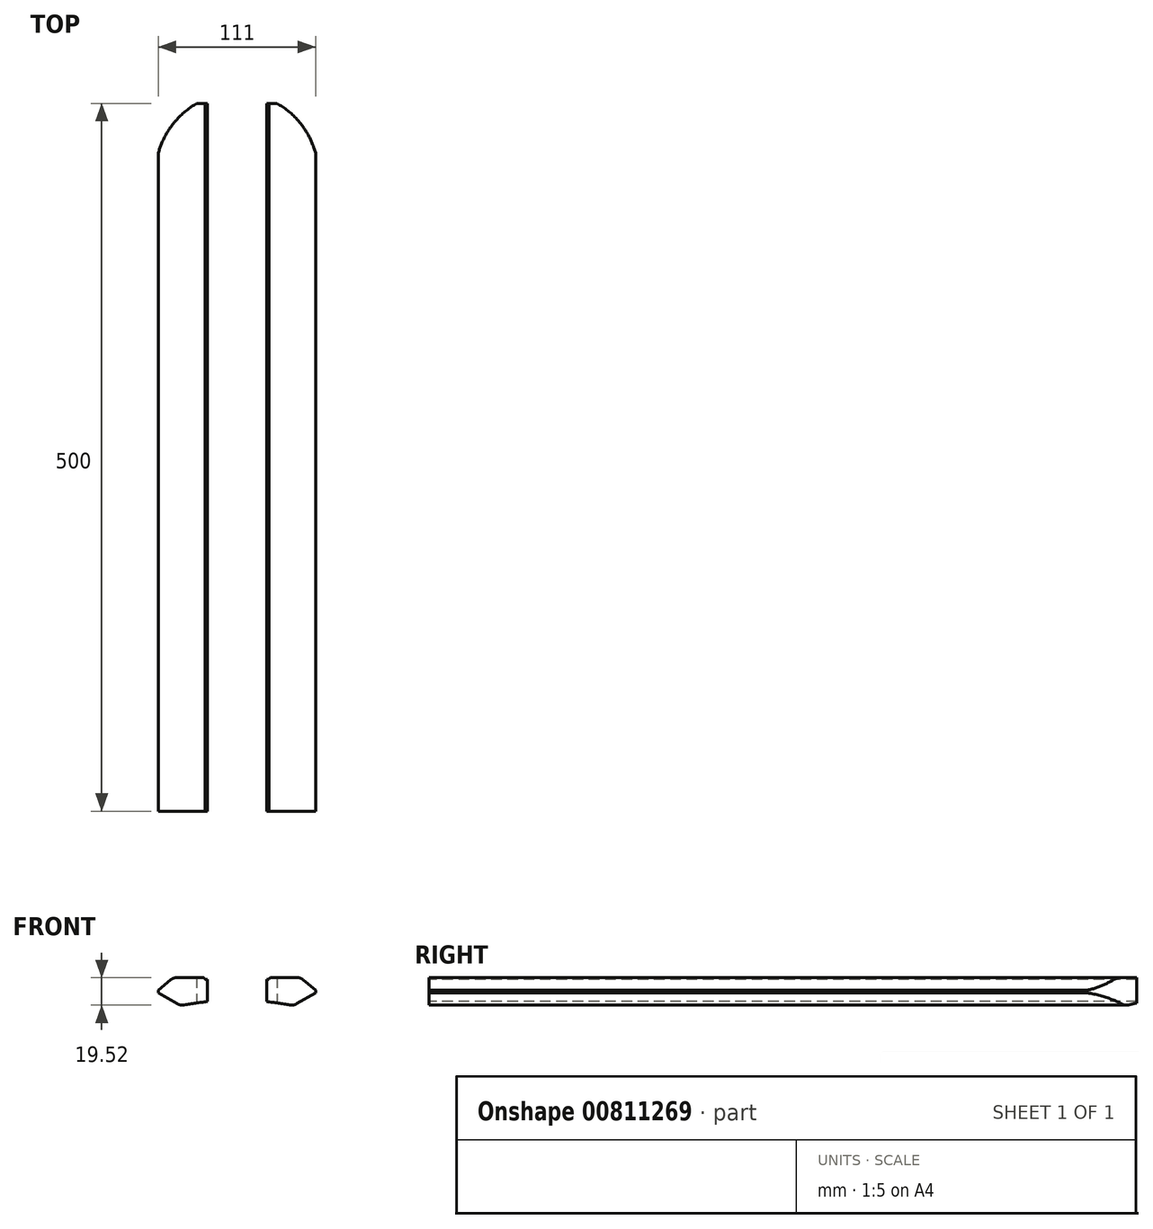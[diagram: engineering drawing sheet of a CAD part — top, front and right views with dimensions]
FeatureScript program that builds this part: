
annotation { "Feature Type Name" : "Feature", "Feature Type Description" : "" }
export const myFeature = defineFeature(function(context is Context, id is Id, definition is map)
    precondition{}
    {
        {
            var Q0;
            Q0=qCreatedBy(makeId("Front.planeOp"),FACE);
            var sketch = newSketch(context, id + "F0", { "sketchPlane" : qUnion([Q0])});
            skLineSegment(sketch, "E0", {"start": v(0, -29.71) * mm, "end": v(0, 39.29) * mm, "construction": true});
            skLineSegment(sketch, "E1", {"start": v(0, 62.32) * mm, "end": v(22.5, 62.32) * mm});
            skLineSegment(sketch, "E2", {"start": v(22.5, 63.62) * mm, "end": v(22.5, 62.32) * mm});
            skLineSegment(sketch, "E3", {"start": v(22.5, 63.62) * mm, "end": v(45.58, 63.62) * mm});
            skLineSegment(sketch, "E4", {"start": v(45.58, 63.62) * mm, "end": v(57.5, 53.62) * mm});
            skLineSegment(sketch, "E5", {"start": v(57.5, 53.62) * mm, "end": v(57.5, 49.62) * mm});
            skLineSegment(sketch, "E6", {"start": v(57.5, 49.62) * mm, "end": v(40.18, 39.62) * mm});
            skLineSegment(sketch, "E7.MirrorCS", {"start": v(0, 62.32) * mm, "end": v(-22.5, 62.32) * mm});
            skLineSegment(sketch, "E8.MirrorCS", {"start": v(-22.5, 63.62) * mm, "end": v(-22.5, 62.32) * mm});
            skLineSegment(sketch, "E9.MirrorCS", {"start": v(-22.5, 63.62) * mm, "end": v(-45.58, 63.62) * mm});
            skLineSegment(sketch, "E10.MirrorCS", {"start": v(-45.58, 63.62) * mm, "end": v(-57.5, 53.62) * mm});
            skLineSegment(sketch, "E11.MirrorCS", {"start": v(-57.5, 53.62) * mm, "end": v(-57.5, 49.62) * mm});
            skLineSegment(sketch, "E12.MirrorCS", {"start": v(-57.5, 49.62) * mm, "end": v(-40.18, 39.62) * mm});
            skArc(sketch, "E13", {"start": v(40.18, 39.62) * mm, "mid": v(0, 43.7) * mm, "end": v(-40.18, 39.62) * mm});
            skSolve(sketch);
        }
        {
            var Q0;
            Q0=makeQuery(id+"F0.imprint","IMPRINT",FACE,{"disambiguationData":[TD([[makeQuery(id+"F0.imprint","IMPRINT",EDGE,{"derivedFrom":sQuery(id+"F0.wireOp",EDGE,"E1")}),-1.0]])]});
            extrude(context, id + "F1", {"entities" : qUnion([Q0]), "endBound" : BoundingType.SYMMETRIC, "depth" : 500 * mm, "offsetDistance" : 25 * mm});
        }
        {
            var Q0;
            Q0=makeQuery(id+"F1.opExtrude","CAP_FACE",FACE,{"disambiguationData":[OSD([sQuery(id+"F0.wireOp",EDGE,"E1"),sQuery(id+"F0.wireOp",EDGE,"E2"),sQuery(id+"F0.wireOp",EDGE,"E3"),sQuery(id+"F0.wireOp",EDGE,"E4"),sQuery(id+"F0.wireOp",EDGE,"E5"),sQuery(id+"F0.wireOp",EDGE,"E6"),sQuery(id+"F0.wireOp",EDGE,"E7.MirrorCS"),sQuery(id+"F0.wireOp",EDGE,"E8.MirrorCS"),sQuery(id+"F0.wireOp",EDGE,"E9.MirrorCS"),sQuery(id+"F0.wireOp",EDGE,"E10.MirrorCS"),sQuery(id+"F0.wireOp",EDGE,"E11.MirrorCS"),sQuery(id+"F0.wireOp",EDGE,"E12.MirrorCS"),sQuery(id+"F0.wireOp",EDGE,"E13")])],"isStart":false});
            var sketch = newSketch(context, id + "F2", { "sketchPlane" : qUnion([Q0])});
            skLineSegment(sketch, "E14.bottom", {"start": v(-19, 60.32) * mm, "end": v(19, 60.32) * mm});
            skLineSegment(sketch, "E14.top", {"start": v(-19, 47.32) * mm, "end": v(19, 47.32) * mm});
            skLineSegment(sketch, "E14.left", {"start": v(-19, 60.32) * mm, "end": v(-19, 47.32) * mm});
            skLineSegment(sketch, "E14.right", {"start": v(19, 60.32) * mm, "end": v(19, 47.32) * mm});
            skPoint(sketch, "E14.middle", {"position": v(0, 53.82) * mm});
            skPoint(sketch, "E14.middle.positionSnap0", {"position": v(0, 62.32) * mm});
            skPoint(sketch, "E14.centerSnap0", {"position": v(0, 62.32) * mm});
            skSolve(sketch);
        }
        {
            var Q0;
            Q0=makeQuery(id+"F2.imprint","IMPRINT",FACE,{"disambiguationData":[TD([[makeQuery(id+"F2.imprint","IMPRINT",EDGE,{"derivedFrom":sQuery(id+"F2.wireOp",EDGE,"E14.bottom")}),-1.0]])]});
            extrude(context, id + "F3", {"entities" : qUnion([Q0]), "operationType" : NewBodyOperationType.REMOVE, "oppositeDirection" : true, "depth" : 1200 * mm, "offsetDistance" : 25 * mm});
        }
        {
            var Q0;
            Q0=makeQuery(id+"F1.opExtrude","SWEPT_EDGE",EDGE,{"disambiguationData":[OSD([sQuery(id+"F0.wireOp",EDGE,"E8.MirrorCS"),sQuery(id+"F0.wireOp",EDGE,"E9.MirrorCS")])]});
            var Q1;
            Q1=makeQuery(id+"F1.opExtrude","SWEPT_EDGE",EDGE,{"disambiguationData":[OSD([sQuery(id+"F0.wireOp",EDGE,"E2"),sQuery(id+"F0.wireOp",EDGE,"E3")])]});
            fillet(context, id + "F4", {"entities" : qUnion([Q0, Q1]), "radius" : 2 * mm, "tangentPropagation" : true, "allowEdgeOverflow" : false});
        }
        {
            var Q0;
            Q0=makeQuery(id+"F1.opExtrude","SWEPT_EDGE",EDGE,{"disambiguationData":[OSD([sQuery(id+"F0.wireOp",EDGE,"E3"),sQuery(id+"F0.wireOp",EDGE,"E4")])]});
            var Q1;
            Q1=makeQuery(id+"F1.opExtrude","SWEPT_EDGE",EDGE,{"disambiguationData":[OSD([sQuery(id+"F0.wireOp",EDGE,"E6"),sQuery(id+"F0.wireOp",EDGE,"E13")])]});
            var Q2;
            Q2=makeQuery(id+"F1.opExtrude","SWEPT_EDGE",EDGE,{"disambiguationData":[OSD([sQuery(id+"F0.wireOp",EDGE,"E12.MirrorCS"),sQuery(id+"F0.wireOp",EDGE,"E13")])]});
            var Q3;
            Q3=makeQuery(id+"F1.opExtrude","SWEPT_EDGE",EDGE,{"disambiguationData":[OSD([sQuery(id+"F0.wireOp",EDGE,"E9.MirrorCS"),sQuery(id+"F0.wireOp",EDGE,"E10.MirrorCS")])]});
            fillet(context, id + "F5", {"entities" : qUnion([Q0, Q1, Q2, Q3]), "radius" : 9 * mm, "tangentPropagation" : true, "allowEdgeOverflow" : false});
        }
        {
            var Q0;
            Q0=makeQuery(id+"F1.opExtrude","SWEPT_EDGE",EDGE,{"disambiguationData":[OSD([sQuery(id+"F0.wireOp",EDGE,"E10.MirrorCS"),sQuery(id+"F0.wireOp",EDGE,"E11.MirrorCS")])]});
            var Q1;
            Q1=makeQuery(id+"F1.opExtrude","SWEPT_EDGE",EDGE,{"disambiguationData":[OSD([sQuery(id+"F0.wireOp",EDGE,"E11.MirrorCS"),sQuery(id+"F0.wireOp",EDGE,"E12.MirrorCS")])]});
            var Q2;
            Q2=makeQuery(id+"F1.opExtrude","SWEPT_EDGE",EDGE,{"disambiguationData":[OSD([sQuery(id+"F0.wireOp",EDGE,"E4"),sQuery(id+"F0.wireOp",EDGE,"E5")])]});
            var Q3;
            Q3=makeQuery(id+"F1.opExtrude","SWEPT_EDGE",EDGE,{"disambiguationData":[OSD([sQuery(id+"F0.wireOp",EDGE,"E5"),sQuery(id+"F0.wireOp",EDGE,"E6")])]});
            fillet(context, id + "F6", {"entities" : qUnion([Q0, Q1, Q2, Q3]), "radius" : 1 * mm, "tangentPropagation" : true, "allowEdgeOverflow" : false});
        }
        {
            var Q0;
            Q0=makeQuery(id+"F1.opExtrude","SWEPT_BODY",BODY,{"disambiguationData":[OSD([sQuery(id+"F0.wireOp",EDGE,"E1"),sQuery(id+"F0.wireOp",EDGE,"E2"),sQuery(id+"F0.wireOp",EDGE,"E3"),sQuery(id+"F0.wireOp",EDGE,"E4"),sQuery(id+"F0.wireOp",EDGE,"E5"),sQuery(id+"F0.wireOp",EDGE,"E6"),sQuery(id+"F0.wireOp",EDGE,"E7.MirrorCS"),sQuery(id+"F0.wireOp",EDGE,"E8.MirrorCS"),sQuery(id+"F0.wireOp",EDGE,"E9.MirrorCS"),sQuery(id+"F0.wireOp",EDGE,"E10.MirrorCS"),sQuery(id+"F0.wireOp",EDGE,"E11.MirrorCS"),sQuery(id+"F0.wireOp",EDGE,"E12.MirrorCS"),sQuery(id+"F0.wireOp",EDGE,"E13")])]});
            transform(context, id + "F7", {"entities" : qUnion([Q0]), "transformType" : TransformType.TRANSLATION_3D, "dx" : 0 * mm, "dy" : 0 * mm, "dz" : -39.8 * mm, "makeCopy" : false});
        }
        {
            var Q0;
            Q0=makeQuery(id+"F1.opExtrude","CAP_FACE",FACE,{"disambiguationData":[OSD([sQuery(id+"F0.wireOp",EDGE,"E1"),sQuery(id+"F0.wireOp",EDGE,"E2"),sQuery(id+"F0.wireOp",EDGE,"E3"),sQuery(id+"F0.wireOp",EDGE,"E4"),sQuery(id+"F0.wireOp",EDGE,"E5"),sQuery(id+"F0.wireOp",EDGE,"E6"),sQuery(id+"F0.wireOp",EDGE,"E7.MirrorCS"),sQuery(id+"F0.wireOp",EDGE,"E8.MirrorCS"),sQuery(id+"F0.wireOp",EDGE,"E9.MirrorCS"),sQuery(id+"F0.wireOp",EDGE,"E10.MirrorCS"),sQuery(id+"F0.wireOp",EDGE,"E11.MirrorCS"),sQuery(id+"F0.wireOp",EDGE,"E12.MirrorCS"),sQuery(id+"F0.wireOp",EDGE,"E13")])],"isStart":false});
            var sketch = newSketch(context, id + "F8", { "sketchPlane" : qUnion([Q0])});
            skLineSegment(sketch, "E15.0.0", {"start": v(43.1, 1.5) * mm, "end": v(57, 9.53) * mm});
            skArc(sketch, "E15.0.1", {"start": v(57, 9.53) * mm, "mid": v(57.37, 9.9) * mm, "end": v(57.5, 10.4) * mm});
            skLineSegment(sketch, "E15.0.2", {"start": v(57.5, 10.4) * mm, "end": v(57.5, 13.35) * mm});
            skArc(sketch, "E15.0.3", {"start": v(57.5, 13.35) * mm, "mid": v(57.4, 13.78) * mm, "end": v(57.14, 14.12) * mm});
            skLineSegment(sketch, "E15.0.4", {"start": v(57.14, 14.12) * mm, "end": v(48.1, 21.71) * mm});
            skArc(sketch, "E15.0.5", {"start": v(48.1, 21.71) * mm, "mid": v(45.38, 23.28) * mm, "end": v(42.3, 23.82) * mm});
            skLineSegment(sketch, "E15.0.6", {"start": v(42.3, 23.82) * mm, "end": v(24.37, 23.82) * mm});
            skArc(sketch, "E15.0.7", {"start": v(24.37, 23.82) * mm, "mid": v(23.23, 23.46) * mm, "end": v(22.5, 22.52) * mm});
            skLineSegment(sketch, "E15.0.8", {"start": v(22.5, 22.52) * mm, "end": v(-22.5, 22.52) * mm});
            skArc(sketch, "E15.0.9", {"start": v(-22.5, 22.52) * mm, "mid": v(-23.23, 23.46) * mm, "end": v(-24.37, 23.82) * mm});
            skLineSegment(sketch, "E15.0.10", {"start": v(-24.37, 23.82) * mm, "end": v(-42.3, 23.82) * mm});
            skArc(sketch, "E15.0.11", {"start": v(-42.3, 23.82) * mm, "mid": v(-45.38, 23.28) * mm, "end": v(-48.1, 21.71) * mm});
            skLineSegment(sketch, "E15.0.12", {"start": v(-48.1, 21.71) * mm, "end": v(-57.14, 14.12) * mm});
            skArc(sketch, "E15.0.13", {"start": v(-57.14, 14.12) * mm, "mid": v(-57.4, 13.78) * mm, "end": v(-57.5, 13.35) * mm});
            skLineSegment(sketch, "E15.0.14", {"start": v(-57.5, 13.35) * mm, "end": v(-57.5, 10.4) * mm});
            skArc(sketch, "E15.0.15", {"start": v(-57.5, 10.4) * mm, "mid": v(-57.37, 9.9) * mm, "end": v(-57, 9.53) * mm});
            skLineSegment(sketch, "E15.0.16", {"start": v(-57, 9.53) * mm, "end": v(-43.1, 1.5) * mm});
            skArc(sketch, "E15.0.17", {"start": v(-43.1, 1.5) * mm, "mid": v(-40.12, 0.43) * mm, "end": v(-36.94, 0.46) * mm});
            skArc(sketch, "E15.0.18", {"start": v(-36.94, 0.46) * mm, "mid": v(0, 3.9) * mm, "end": v(36.94, 0.46) * mm});
            skArc(sketch, "E15.0.19", {"start": v(36.94, 0.46) * mm, "mid": v(40.12, 0.43) * mm, "end": v(43.1, 1.5) * mm});
            skArc(sketch, "E16.0", {"start": v(-37.3, 2.42) * mm, "mid": v(-29.18, 3.78) * mm, "end": v(-21, 4.8) * mm});
            skArc(sketch, "E16.1", {"start": v(-42.1, 3.24) * mm, "mid": v(-39.78, 2.4) * mm, "end": v(-37.3, 2.42) * mm});
            skLineSegment(sketch, "E16.2", {"start": v(-55.5, 10.98) * mm, "end": v(-42.1, 3.24) * mm});
            skLineSegment(sketch, "E16.3", {"start": v(-55.5, 12.89) * mm, "end": v(-55.5, 10.98) * mm});
            skLineSegment(sketch, "E16.4", {"start": v(-24.37, 21.82) * mm, "end": v(-24.37, 21.82) * mm});
            skLineSegment(sketch, "E16.5", {"start": v(-24.37, 21.82) * mm, "end": v(-42.3, 21.82) * mm});
            skArc(sketch, "E16.6", {"start": v(-42.3, 21.82) * mm, "mid": v(-44.7, 21.4) * mm, "end": v(-46.8, 20.18) * mm});
            skLineSegment(sketch, "E16.7", {"start": v(-46.8, 20.18) * mm, "end": v(-55.5, 12.89) * mm});
            skLineSegment(sketch, "E17.0", {"start": v(-21, 20.52) * mm, "end": v(-21, 4.8) * mm});
            skLineSegment(sketch, "E18.0", {"start": v(-21, 20.52) * mm, "end": v(-22.5, 20.52) * mm});
            skArc(sketch, "E19", {"start": v(-22.5, 20.52) * mm, "mid": v(-23.23, 21.46) * mm, "end": v(-24.37, 21.82) * mm});
            skArc(sketch, "E20.MirrorCS", {"start": v(22.5, 20.52) * mm, "mid": v(23.23, 21.46) * mm, "end": v(24.37, 21.82) * mm});
            skLineSegment(sketch, "E21.MirrorCS", {"start": v(24.37, 21.82) * mm, "end": v(42.3, 21.82) * mm});
            skArc(sketch, "E22.MirrorCS", {"start": v(42.3, 21.82) * mm, "mid": v(44.7, 21.4) * mm, "end": v(46.8, 20.18) * mm});
            skLineSegment(sketch, "E23.MirrorCS", {"start": v(46.8, 20.18) * mm, "end": v(55.5, 12.89) * mm});
            skLineSegment(sketch, "E24.MirrorCS", {"start": v(55.5, 12.89) * mm, "end": v(55.5, 10.98) * mm});
            skLineSegment(sketch, "E25.MirrorCS", {"start": v(55.5, 10.98) * mm, "end": v(42.1, 3.24) * mm});
            skArc(sketch, "E26.MirrorCS", {"start": v(42.1, 3.24) * mm, "mid": v(39.78, 2.4) * mm, "end": v(37.3, 2.42) * mm});
            skArc(sketch, "E27.MirrorCS", {"start": v(37.3, 2.42) * mm, "mid": v(29.18, 3.78) * mm, "end": v(21, 4.8) * mm});
            skLineSegment(sketch, "E28.MirrorCS", {"start": v(21, 20.52) * mm, "end": v(21, 4.8) * mm});
            skLineSegment(sketch, "E29.MirrorCS", {"start": v(21, 20.52) * mm, "end": v(22.5, 20.52) * mm});
            skSolve(sketch);
        }
        {
            var Q0;
            Q0=makeQuery(id+"F8.imprint","IMPRINT",FACE,{"disambiguationData":[TD([[makeQuery(id+"F8.imprint","IMPRINT",EDGE,{"derivedFrom":sQuery(id+"F8.wireOp",EDGE,"E16.0")}),1.0]])]});
            var Q1;
            Q1=makeQuery(id+"F8.imprint","IMPRINT",FACE,{"disambiguationData":[TD([[makeQuery(id+"F8.imprint","IMPRINT",EDGE,{"derivedFrom":sQuery(id+"F8.wireOp",EDGE,"E20.MirrorCS")}),-1.0]])]});
            extrude(context, id + "F9", {"entities" : qUnion([Q0, Q1]), "operationType" : NewBodyOperationType.REMOVE, "endBound" : BoundingType.THROUGH_ALL, "oppositeDirection" : true, "depth" : 25 * mm, "offsetDistance" : 25 * mm});
        }
        {
            var Q0;
            Q0=qCreatedBy(makeId("Top.planeOp"),FACE);
            var sketch = newSketch(context, id + "F10", { "sketchPlane" : qUnion([Q0])});
            skArc(sketch, "E30", {"start": v(57.5, 200) * mm, "mid": v(0, 257.5) * mm, "end": v(-57.5, 200) * mm});
            skLineSegment(sketch, "E31", {"start": v(-57.5, 200) * mm, "end": v(-57.5, 280) * mm});
            skLineSegment(sketch, "E32", {"start": v(57.5, 200) * mm, "end": v(57.5, 280) * mm});
            skLineSegment(sketch, "E33", {"start": v(57.5, 280) * mm, "end": v(-57.5, 280) * mm});
            skSolve(sketch);
        }
        {
            var Q0;
            Q0=makeQuery(id+"F10.imprint","IMPRINT",FACE,{"disambiguationData":[TD([[makeQuery(id+"F10.imprint","IMPRINT",EDGE,{"derivedFrom":sQuery(id+"F10.wireOp",EDGE,"E30")}),-1.0]])]});
            extrude(context, id + "F11", {"entities" : qUnion([Q0]), "operationType" : NewBodyOperationType.REMOVE, "endBound" : BoundingType.THROUGH_ALL, "depth" : 25 * mm, "offsetDistance" : 25 * mm, "hasSecondDirection" : true, "secondDirectionBound" : SecondDirectionBoundingType.THROUGH_ALL, "secondDirectionOppositeDirection" : true, "secondDirectionDepth" : 25 * mm});
        }
    });
